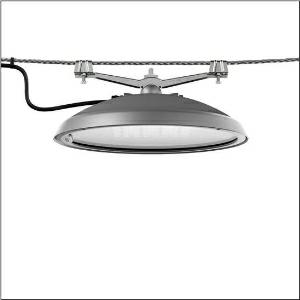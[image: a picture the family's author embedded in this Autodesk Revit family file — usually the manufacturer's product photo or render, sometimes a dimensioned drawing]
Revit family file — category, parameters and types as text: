
# Revit family: dl_r__50_iq_mini___p1_0s_5xa248u31f08fe_9f5a
name_source: partatom
category: Lighting Fixtures
units: mm (PartAtom-declared; Revit-internal decimal feet)

## family parameters
Cut with Voids When Loaded = No
Host = Face
Light Source = No
Part Type = Normal
Room Calculation Point = No
Round Connector Dimension = Use Diameter
Shared = No

## types (1)
- --- (1 x LED, 2610 lm, 16.3 W, 3000K)
    Apparent Load = 16 VA
    CIE Flux Codes = 23 54 93 100 100
    Color Rendering = 70
    Color Temperature = 3000K
    Default Elevation = 1800 mm
    Description = DL® 50 iQ mini, catenary luminaire, primary light control with lens, of PMMA, primary optical cover: cover, of toughened safety glass, transparent, light distribution: P1.0s, light emission: direct distribution, primary light characteristic: symmetric, installation type: suspended mounting, LED, High Power LED, rated luminous flux: 2.610lm, luminous efficacy: 160lm/W, light colour: 730, colour temperature: 3000K, control gear: iQ Street-Remote, control: optimised constant luminous flux control (CLO 2.0), Desk-Remote (wireless, voltage-free reading and setting of iQ features in the workshop via application-optimized NFC function/RFID function), Light-Fading, Smart-Wire, Night-Set, Lumen-Switch, Temp-Guard, Auto-Match, Street-Remote, mains connection: 230..240V, AC, 50/60Hz, start of lifetime: 16W, end of service life: 17W, reduction: 8W, luminaire housing, of diecast aluminium, powder-coated, Siteco® metallic grey (DB 702S), diameter: 500mm, height: 115mm, mounting height: 4..12m, protection rating (complete): IP66, insulation class (complete): insulation class II (safety insulation), certification: CE, ENEC, ENEC+, VDE, impact resistance: IK08, permissible operating ambient temperature for outdoor applications: -25..+40°C, standard-compliant lighting for roads and squares, packaging unit: 1 piece

Light Distribution: P1.0s
    Height = 124 mm  [stored 0.406824 ft]
    Lamp = 1 x LED
    Lamp Light Flux = 2610 lm
    Lamp Power = 16.3 W
    Lamp count = 1
    Length = 500 mm
    Luminous efficacy = 160 lm/W
    Manufacturer = Siteco
    ModVariant = No
    Model = 5XA248U31F08FE
    Number of Poles = 1
    OnlyDefault = Yes
    Power Factor = 1
    Product Name = DL® 50 iQ mini | P1.0s
    Product group = catenary luminaire
    ProductGroupID = 6300
    Protection Class = Protection class II
    Protection Degree = IP 66
    RLX_Detail_Level = 1
    RLX_Emergency_Light_Flux = 0 lm
    RLX_Emergency_Type = 0
    RLX_Emergency_Type_DB = No
    RlxData = <blob elided: 123129 chars, md5=17e03891>
    Socket = socket
    Standby Power = 0 W
    System Light Flux = 2610 lm
    System Power = 16 W
    Type Comments = factory setting: luminous flux: 100 % | dim-lin: 254 | 333 mA
    Type Image = l_1242791.jpg
    URL = http://relux.com
    VarID = @adj_159273
    Voltage = 0 V
    Weight = 0.00 kg
    Width = 0 mm  [stored 0 ft]

note: [stored X ft] marks values corroborated as IEEE doubles in the binary element streams (Revit-internal decimal feet)

## geometry (parser evidence)
native form markers: Blend x4, Sweep x11
no freeform markers — native parametric forms only
